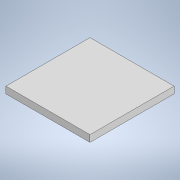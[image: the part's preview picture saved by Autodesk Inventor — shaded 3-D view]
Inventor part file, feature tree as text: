
AUTODESK INVENTOR PART (.ipt)
format: ipt  version: 2022.3 (Build 263350000, 350)  size: 92,672 bytes
history: native  units: in
note: dims shown in document units (in); Inventor stores cm internally (conversion verified against a paired STEP export)
features: extrude x1, sketch x1
ambient origin geometry x8: Origin, YZ Plane, XZ Plane, XY Plane, X Axis, Y Axis, Z Axis, Center Point
bodies: Solid1 (feature_tree)
feature tree (2):
  extrude  "Extrusion1"  [1 undecoded]
  sketch  "Sketch1"  dims[d1=0.1575in d2=0.0in]
note: 1 required parameter value undecoded (feature->parameter linkage not recoverable at this tier; creation-order binding heuristic only, values carry confidence <= 0.55)
